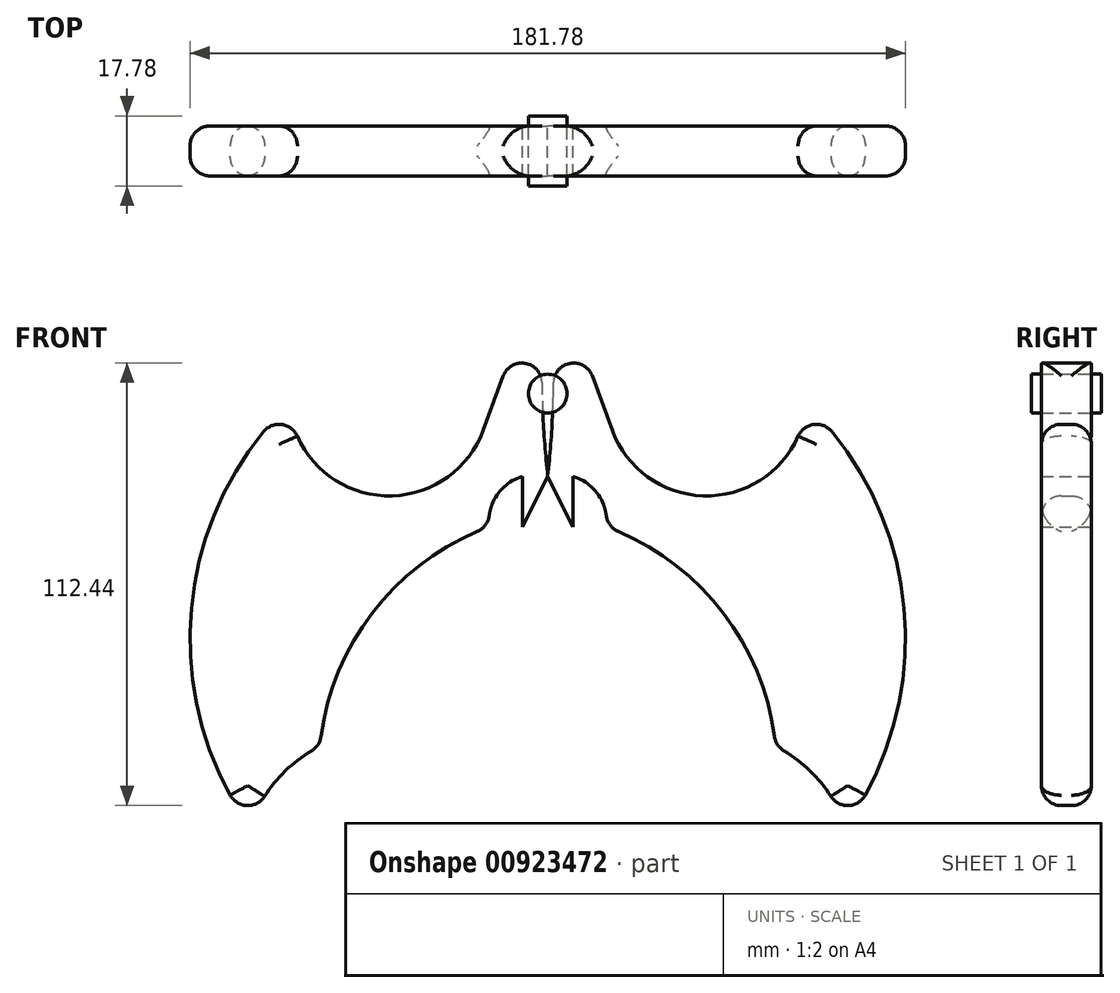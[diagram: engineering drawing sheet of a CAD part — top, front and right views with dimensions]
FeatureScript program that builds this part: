
annotation { "Feature Type Name" : "Feature", "Feature Type Description" : "" }
export const myFeature = defineFeature(function(context is Context, id is Id, definition is map)
    precondition{}
    {
        {
            var Q0;
            Q0=qCreatedBy(makeId("Front.planeOp"),FACE);
            var sketch = newSketch(context, id + "F0", { "sketchPlane" : qUnion([Q0])});
            skLineSegment(sketch, "E0", {"start": v(0, 69.03) * mm, "end": v(-16.4, 24.51) * mm});
            skArc(sketch, "E1", {"start": v(-64.22, 24.51) * mm, "mid": v(-40.3, 7.84) * mm, "end": v(-16.4, 24.51) * mm});
            skArc(sketch, "E2", {"start": v(-64.22, 32.64) * mm, "mid": v(-64.6, 28.58) * mm, "end": v(-64.22, 24.51) * mm});
            skArc(sketch, "E3", {"start": v(-64.22, 32.64) * mm, "mid": v(-90.44, -19.65) * mm, "end": v(-75.65, -76.25) * mm});
            skArc(sketch, "E4", {"start": v(-57.9, -55.8) * mm, "mid": v(-68.8, -64.27) * mm, "end": v(-75.65, -76.25) * mm});
            skArc(sketch, "E5", {"start": v(-14.89, 0) * mm, "mid": v(-44.41, -21.72) * mm, "end": v(-57.9, -55.8) * mm});
            skArc(sketch, "E6", {"start": v(-6.47, 12.78) * mm, "mid": v(-12.99, 7.91) * mm, "end": v(-14.89, 0) * mm});
            skLineSegment(sketch, "E7", {"start": v(-6.47, 12.78) * mm, "end": v(-6.47, 0) * mm});
            skLineSegment(sketch, "E8", {"start": v(-6.47, 0) * mm, "end": v(0, 12.78) * mm});
            skArc(sketch, "E9", {"start": v(0, 69.03) * mm, "mid": v(-1.52, 40.9) * mm, "end": v(0, 12.78) * mm});
            skSolve(sketch);
        }
        {
            var Q0;
            Q0=makeQuery(id+"F0.imprint","IMPRINT",FACE,{"disambiguationData":[TD([[makeQuery(id+"F0.imprint","IMPRINT",EDGE,{"derivedFrom":sQuery(id+"F0.wireOp",EDGE,"E0")}),1.0]])]});
            extrude(context, id + "F1", {"entities" : qUnion([Q0]), "depth" : 12.7 * mm, "offsetDistance" : 25.4 * mm});
        }
        {
            var Q0;
            Q0=makeQuery(id+"F1.opExtrude","SWEPT_FACE",FACE,{"disambiguationData":[OSD([sQuery(id+"F0.wireOp",EDGE,"E0")])]});
            var Q1;
            Q1=makeQuery(id+"F1.opExtrude","SWEPT_FACE",FACE,{"disambiguationData":[OSD([sQuery(id+"F0.wireOp",EDGE,"E5")])]});
            var Q2;
            Q2=makeQuery(id+"F1.opExtrude","SWEPT_FACE",FACE,{"disambiguationData":[OSD([sQuery(id+"F0.wireOp",EDGE,"E4")])]});
            var Q3;
            Q3=makeQuery(id+"F1.opExtrude","SWEPT_FACE",FACE,{"disambiguationData":[OSD([sQuery(id+"F0.wireOp",EDGE,"E1")])]});
            fillet(context, id + "F2", {"entities" : qUnion([Q0, Q1, Q2, Q3]), "radius" : 5.08 * mm, "tangentPropagation" : true, "allowEdgeOverflow" : false});
        }
        {
            var Q0;
            Q0=makeQuery(id+"F1.opExtrude","SWEPT_FACE",FACE,{"disambiguationData":[OSD([sQuery(id+"F0.wireOp",EDGE,"E3")])]});
            fillet(context, id + "F3", {"entities" : qUnion([Q0]), "radius" : 5.08 * mm, "tangentPropagation" : true, "allowEdgeOverflow" : false});
        }
        {
            var Q0;
            Q0=makeQuery(id+"F1.opExtrude","SWEPT_BODY",BODY,{"disambiguationData":[OSD([sQuery(id+"F0.wireOp",EDGE,"E0"),sQuery(id+"F0.wireOp",EDGE,"E1"),sQuery(id+"F0.wireOp",EDGE,"E2"),sQuery(id+"F0.wireOp",EDGE,"E3"),sQuery(id+"F0.wireOp",EDGE,"E4"),sQuery(id+"F0.wireOp",EDGE,"E5"),sQuery(id+"F0.wireOp",EDGE,"E6"),sQuery(id+"F0.wireOp",EDGE,"E7"),sQuery(id+"F0.wireOp",EDGE,"E8"),sQuery(id+"F0.wireOp",EDGE,"E9")])]});
            var Q1;
            Q1=qCreatedBy(makeId("Right.planeOp"),FACE);
            mirror(context, id + "F4", {"entities" : qUnion([Q0]), "mirrorPlane" : qUnion([Q1])});
        }
        {
            var Q0;
            Q0=qCreatedBy(makeId("Front.planeOp"),FACE);
            var sketch = newSketch(context, id + "F5", { "sketchPlane" : qUnion([Q0])});
            skCircle(sketch, "E10", {"center": v(0, 33.84) * mm, "radius": 4.92 * mm});
            skSolve(sketch);
        }
        {
            var Q0;
            Q0=makeQuery(id+"F5.imprint","IMPRINT",FACE,{"disambiguationData":[TD([[makeQuery(id+"F5.imprint","IMPRINT",EDGE,{"derivedFrom":sQuery(id+"F5.wireOp",EDGE,"E10")}),1.0]])]});
            extrude(context, id + "F6", {"entities" : qUnion([Q0]), "depth" : 15.24 * mm, "offsetDistance" : 25.4 * mm, "hasSecondDirection" : true, "secondDirectionOppositeDirection" : true, "secondDirectionDepth" : 2.54 * mm});
        }
    });
